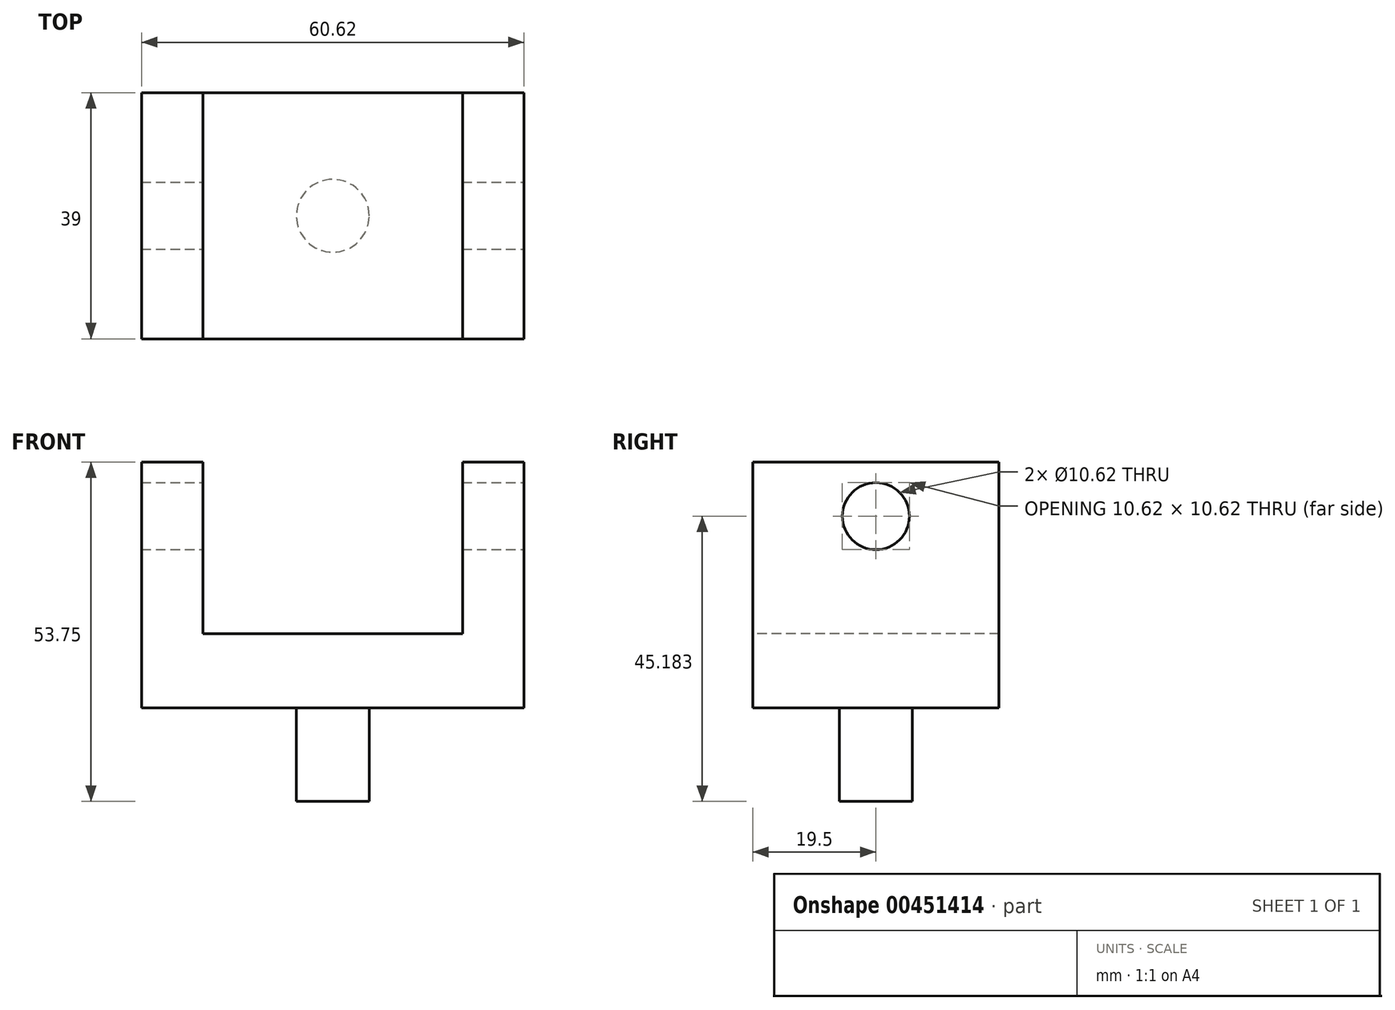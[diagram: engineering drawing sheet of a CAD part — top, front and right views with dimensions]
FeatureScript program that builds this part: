
annotation { "Feature Type Name" : "Feature", "Feature Type Description" : "" }
export const myFeature = defineFeature(function(context is Context, id is Id, definition is map)
    precondition{}
    {
        {
            var Q0;
            Q0=qCreatedBy(makeId("Front.planeOp"),FACE);
            var sketch = newSketch(context, id + "F0", { "sketchPlane" : qUnion([Q0])});
            skLineSegment(sketch, "E0", {"start": v(0, -2.57) * mm, "end": v(30.31, -2.57) * mm});
            skLineSegment(sketch, "E1", {"start": v(30.31, -2.57) * mm, "end": v(30.31, 36.38) * mm});
            skLineSegment(sketch, "E2", {"start": v(30.31, 36.38) * mm, "end": v(20.55, 36.38) * mm});
            skLineSegment(sketch, "E3", {"start": v(20.55, 36.38) * mm, "end": v(20.55, 9.2) * mm});
            skLineSegment(sketch, "E4", {"start": v(20.55, 9.2) * mm, "end": v(0, 9.2) * mm});
            skLineSegment(sketch, "E5", {"start": v(0, 9.2) * mm, "end": v(0, -2.57) * mm});
            skSolve(sketch);
        }
        {
            var Q0;
            Q0=makeQuery(id+"F0.imprint","IMPRINT",FACE,{"disambiguationData":[TD([[makeQuery(id+"F0.imprint","IMPRINT",EDGE,{"derivedFrom":sQuery(id+"F0.wireOp",EDGE,"E0")}),1.0]])]});
            extrude(context, id + "F1", {"entities" : qUnion([Q0]), "oppositeDirection" : true, "depth" : 39 * mm});
        }
        {
            var Q0;
            Q0=makeQuery(id+"F1.opExtrude","SWEPT_BODY",BODY,{"disambiguationData":[OSD([sQuery(id+"F0.wireOp",EDGE,"E0"),sQuery(id+"F0.wireOp",EDGE,"E1"),sQuery(id+"F0.wireOp",EDGE,"E2"),sQuery(id+"F0.wireOp",EDGE,"E3"),sQuery(id+"F0.wireOp",EDGE,"E4"),sQuery(id+"F0.wireOp",EDGE,"E5")])]});
            var Q1;
            Q1=makeQuery(id+"F1.opExtrude","SWEPT_FACE",FACE,{"disambiguationData":[OSD([sQuery(id+"F0.wireOp",EDGE,"E5")])]});
            mirror(context, id + "F2", {"operationType" : NewBodyOperationType.ADD, "entities" : qUnion([Q0]), "mirrorPlane" : qUnion([Q1])});
        }
        {
            var Q0;
            Q0=makeQuery(id+"F1.opExtrude","SWEPT_FACE",FACE,{"disambiguationData":[OSD([sQuery(id+"F0.wireOp",EDGE,"E1")])]});
            var sketch = newSketch(context, id + "F3", { "sketchPlane" : qUnion([Q0])});
            skCircle(sketch, "E6", {"center": v(19.5, 27.81) * mm, "radius": 5.3 * mm});
            skPoint(sketch, "E6.centerSnap0", {"position": v(19.5, 36.38) * mm});
            skSolve(sketch);
        }
        {
            var Q0;
            Q0=makeQuery(id+"F3.imprint","IMPRINT",FACE,{"disambiguationData":[TD([[makeQuery(id+"F3.imprint","IMPRINT",EDGE,{"derivedFrom":sQuery(id+"F3.wireOp",EDGE,"E6")}),1.0]])]});
            extrude(context, id + "F4", {"entities" : qUnion([Q0]), "operationType" : NewBodyOperationType.REMOVE, "endBound" : BoundingType.THROUGH_ALL, "oppositeDirection" : true, "depth" : 111.5 * mm});
        }
        {
            var Q0;
            {var subQ0=makeQuery(id+"F1.opExtrude","SWEPT_FACE",FACE,{"disambiguationData":[OSD([sQuery(id+"F0.wireOp",EDGE,"E0")])]});Q0=makeQuery(id+"F2.boolean.opBoolean","MERGE",FACE,{"derivedFrom":[subQ0,makeQuery(id+"F2.opPattern","COPY",FACE,{"derivedFrom":subQ0,"instanceName":"1"})]});}
            var sketch = newSketch(context, id + "F5", { "sketchPlane" : qUnion([Q0])});
            skCircle(sketch, "E7", {"center": v(0, -19.5) * mm, "radius": 5.77 * mm});
            skPoint(sketch, "E7.centerSnap0", {"position": v(30.31, -19.5) * mm});
            skSolve(sketch);
        }
        {
            var Q0;
            Q0=makeQuery(id+"F5.imprint","IMPRINT",FACE,{"disambiguationData":[TD([[makeQuery(id+"F5.imprint","IMPRINT",EDGE,{"derivedFrom":sQuery(id+"F5.wireOp",EDGE,"E7")}),1.0]])]});
            extrude(context, id + "F6", {"entities" : qUnion([Q0]), "operationType" : NewBodyOperationType.ADD, "depth" : 14.8 * mm});
        }
    });
